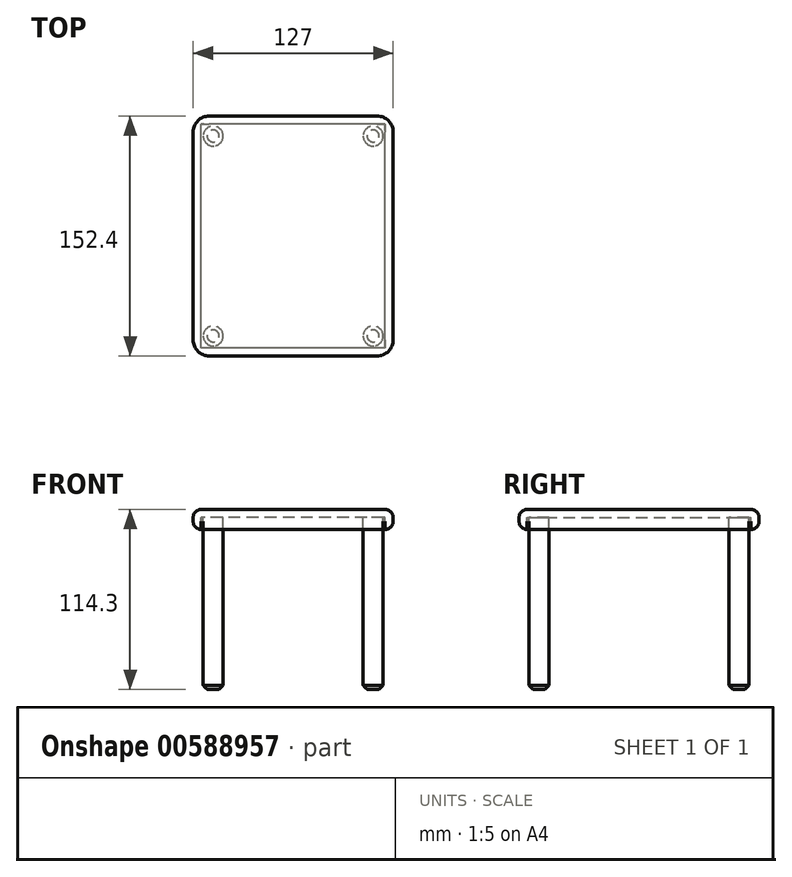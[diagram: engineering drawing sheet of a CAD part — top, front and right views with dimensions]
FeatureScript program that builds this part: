
annotation { "Feature Type Name" : "Feature", "Feature Type Description" : "" }
export const myFeature = defineFeature(function(context is Context, id is Id, definition is map)
    precondition{}
    {
        {
            var Q0;
            Q0=qCreatedBy(makeId("Top.planeOp"),FACE);
            var sketch = newSketch(context, id + "F0", { "sketchPlane" : qUnion([Q0])});
            skLineSegment(sketch, "E0.bottom", {"start": v(63.5, -76.2) * mm, "end": v(-63.5, -76.2) * mm});
            skLineSegment(sketch, "E0.top", {"start": v(63.5, 76.2) * mm, "end": v(-63.5, 76.2) * mm});
            skLineSegment(sketch, "E0.left", {"start": v(63.5, -76.2) * mm, "end": v(63.5, 76.2) * mm});
            skLineSegment(sketch, "E0.right", {"start": v(-63.5, -76.2) * mm, "end": v(-63.5, 76.2) * mm});
            skPoint(sketch, "E0.middle", {"position": v(0, 0) * mm});
            skSolve(sketch);
        }
        {
            var Q0;
            Q0=makeQuery(id+"F0.imprint","IMPRINT",FACE,{"disambiguationData":[TD([[makeQuery(id+"F0.imprint","IMPRINT",EDGE,{"derivedFrom":sQuery(id+"F0.wireOp",EDGE,"E0.bottom")}),-1.0]])]});
            extrude(context, id + "F1", {"entities" : qUnion([Q0]), "oppositeDirection" : true, "depth" : 12.7 * mm, "offsetDistance" : 25.4 * mm});
        }
        {
            var Q0;
            Q0=makeQuery(id+"F1.opExtrude","CAP_FACE",FACE,{"disambiguationData":[OSD([sQuery(id+"F0.wireOp",EDGE,"E0.bottom"),sQuery(id+"F0.wireOp",EDGE,"E0.top"),sQuery(id+"F0.wireOp",EDGE,"E0.left"),sQuery(id+"F0.wireOp",EDGE,"E0.right")])],"isStart":false});
            shell(context, id + "F2", {"entities" : qUnion([Q0]), "thickness" : 5.08 * mm});
        }
        {
            var Q0;
            Q0=makeQuery(id+"F1.opExtrude","CAP_FACE",FACE,{"disambiguationData":[OSD([sQuery(id+"F0.wireOp",EDGE,"E0.bottom"),sQuery(id+"F0.wireOp",EDGE,"E0.top"),sQuery(id+"F0.wireOp",EDGE,"E0.left"),sQuery(id+"F0.wireOp",EDGE,"E0.right")])],"isStart":false});
            var sketch = newSketch(context, id + "F3", { "sketchPlane" : qUnion([Q0])});
            skCircle(sketch, "E1", {"center": v(-50.8, -63.5) * mm, "radius": 6.35 * mm});
            skCircle(sketch, "E2", {"center": v(50.8, -63.5) * mm, "radius": 6.35 * mm});
            skCircle(sketch, "E3", {"center": v(50.8, 63.5) * mm, "radius": 6.35 * mm});
            skCircle(sketch, "E4", {"center": v(-50.8, 63.5) * mm, "radius": 6.35 * mm});
            skSolve(sketch);
        }
        {
            var Q0;
            Q0=makeQuery(id+"F3.imprint","IMPRINT",FACE,{"disambiguationData":[TD([[makeQuery(id+"F3.imprint","IMPRINT",EDGE,{"derivedFrom":sQuery(id+"F3.wireOp",EDGE,"E4")}),1.0]])]});
            var Q1;
            Q1=makeQuery(id+"F3.imprint","IMPRINT",FACE,{"disambiguationData":[TD([[makeQuery(id+"F3.imprint","IMPRINT",EDGE,{"derivedFrom":sQuery(id+"F3.wireOp",EDGE,"E3")}),1.0]])]});
            var Q2;
            Q2=makeQuery(id+"F3.imprint","IMPRINT",FACE,{"disambiguationData":[TD([[makeQuery(id+"F3.imprint","IMPRINT",EDGE,{"derivedFrom":sQuery(id+"F3.wireOp",EDGE,"E2")}),1.0]])]});
            var Q3;
            Q3=makeQuery(id+"F3.imprint","IMPRINT",FACE,{"disambiguationData":[TD([[makeQuery(id+"F3.imprint","IMPRINT",EDGE,{"derivedFrom":sQuery(id+"F3.wireOp",EDGE,"E1")}),1.0]])]});
            var Q4;
            Q4=makeQuery(id+"F2.opShell","OFFSET_FACE",FACE,{"disambiguationData":[OSD([sQuery(id+"F0.wireOp",EDGE,"E0.bottom"),sQuery(id+"F0.wireOp",EDGE,"E0.top"),sQuery(id+"F0.wireOp",EDGE,"E0.left"),sQuery(id+"F0.wireOp",EDGE,"E0.right")])]});
            extrude(context, id + "F4", {"entities" : qUnion([Q0, Q1, Q2, Q3]), "operationType" : NewBodyOperationType.ADD, "depth" : 101.6 * mm, "offsetDistance" : 25.4 * mm, "hasSecondDirection" : true, "secondDirectionBound" : SecondDirectionBoundingType.UP_TO_SURFACE, "secondDirectionOppositeDirection" : true, "secondDirectionDepth" : 25.4 * mm, "secondDirectionBoundEntityFace" : qUnion([Q4])});
        }
        {
            var Q0;
            Q0=makeQuery(id+"F1.opExtrude","SWEPT_EDGE",EDGE,{"disambiguationData":[OSD([sQuery(id+"F0.wireOp",EDGE,"E0.bottom"),sQuery(id+"F0.wireOp",EDGE,"E0.right")])]});
            var Q1;
            Q1=makeQuery(id+"F1.opExtrude","SWEPT_EDGE",EDGE,{"disambiguationData":[OSD([sQuery(id+"F0.wireOp",EDGE,"E0.top"),sQuery(id+"F0.wireOp",EDGE,"E0.right")])]});
            var Q2;
            Q2=makeQuery(id+"F1.opExtrude","SWEPT_EDGE",EDGE,{"disambiguationData":[OSD([sQuery(id+"F0.wireOp",EDGE,"E0.top"),sQuery(id+"F0.wireOp",EDGE,"E0.left")])]});
            var Q3;
            Q3=makeQuery(id+"F1.opExtrude","SWEPT_EDGE",EDGE,{"disambiguationData":[OSD([sQuery(id+"F0.wireOp",EDGE,"E0.bottom"),sQuery(id+"F0.wireOp",EDGE,"E0.left")])]});
            fillet(context, id + "F5", {"entities" : qUnion([Q0, Q1, Q2, Q3]), "radius" : 10.16 * mm, "tangentPropagation" : true, "allowEdgeOverflow" : false});
        }
        {
            var Q0;
            Q0=makeQuery(id+"F1.opExtrude","SWEPT_FACE",FACE,{"disambiguationData":[OSD([sQuery(id+"F0.wireOp",EDGE,"E0.right")])]});
            fillet(context, id + "F6", {"entities" : qUnion([Q0]), "radius" : 5.08 * mm, "tangentPropagation" : true, "allowEdgeOverflow" : false});
        }
        {
            var Q0;
            Q0=makeQuery(id+"F4.opExtrude","CAP_FACE",FACE,{"disambiguationData":[OSD([sQuery(id+"F3.wireOp",EDGE,"E4")])],"isStart":false});
            var Q1;
            Q1=makeQuery(id+"F4.opExtrude","CAP_FACE",FACE,{"disambiguationData":[OSD([sQuery(id+"F3.wireOp",EDGE,"E3")])],"isStart":false});
            var Q2;
            Q2=makeQuery(id+"F4.opExtrude","CAP_FACE",FACE,{"disambiguationData":[OSD([sQuery(id+"F3.wireOp",EDGE,"E1")])],"isStart":false});
            var Q3;
            Q3=makeQuery(id+"F4.opExtrude","CAP_FACE",FACE,{"disambiguationData":[OSD([sQuery(id+"F3.wireOp",EDGE,"E2")])],"isStart":false});
            chamfer(context, id + "F7", {"entities" : qUnion([Q0, Q1, Q2, Q3]), "width" : 2.54 * mm, "tangentPropagation" : true});
        }
    });
